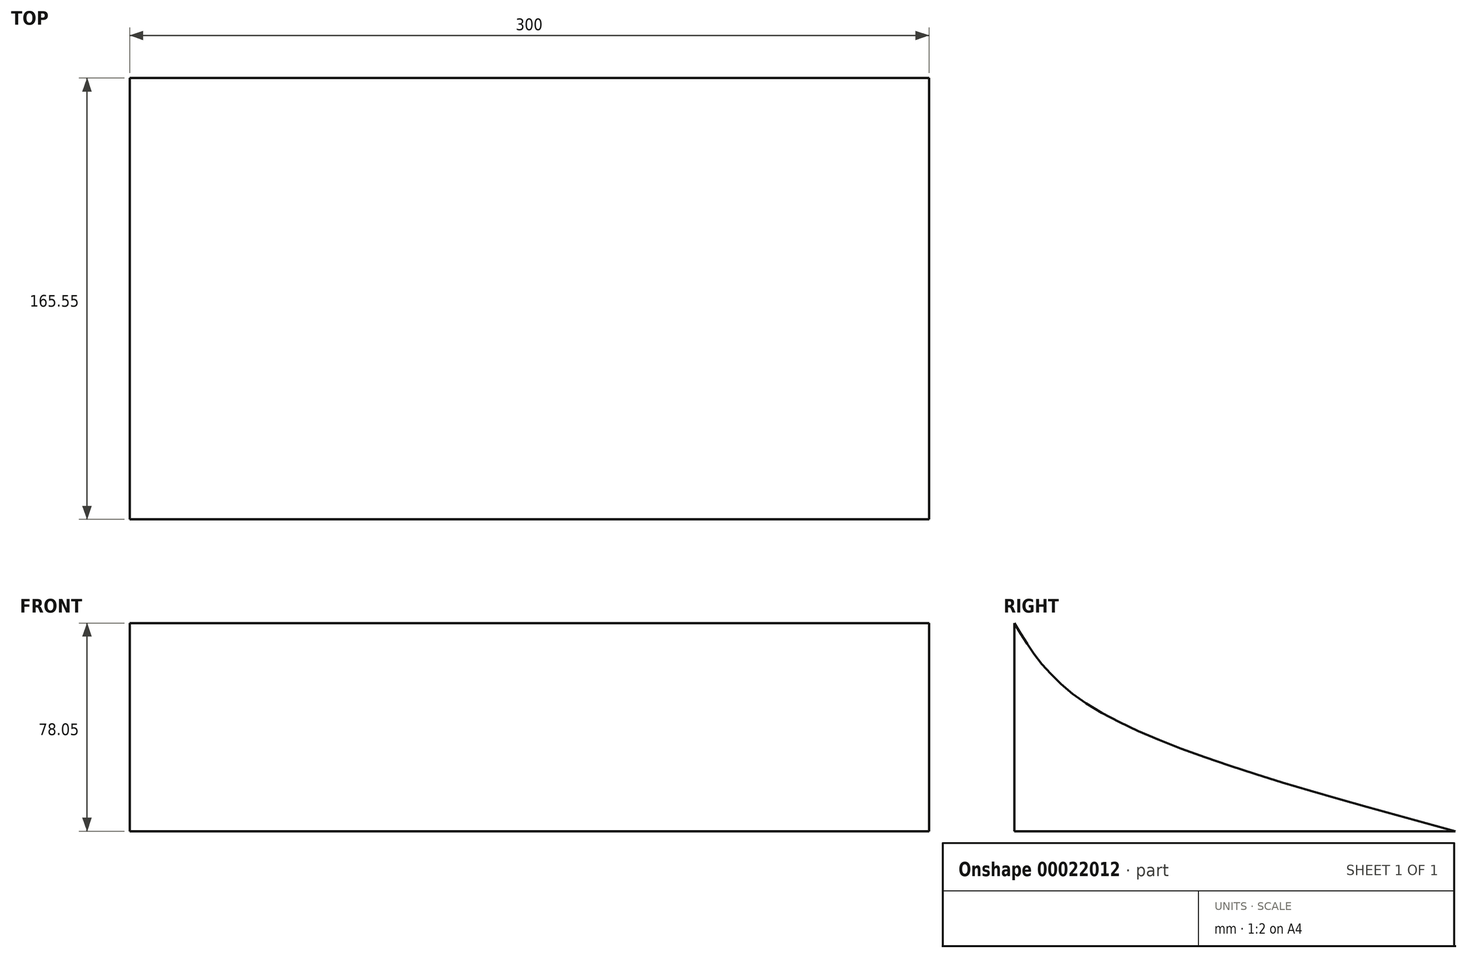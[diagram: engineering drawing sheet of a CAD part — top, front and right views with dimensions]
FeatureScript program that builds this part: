
annotation { "Feature Type Name" : "Feature", "Feature Type Description" : "" }
export const myFeature = defineFeature(function(context is Context, id is Id, definition is map)
    precondition{}
    {
        {
            var Q0;
            Q0=qCreatedBy(makeId("Right.planeOp"),FACE);
            var sketch = newSketch(context, id + "F0", { "sketchPlane" : qUnion([Q0])});
            skFitSpline(sketch, "E0", {"points": [v(0, 0) * mm, v(26.1, -29.47) * mm, v(165.55, -78.05) * mm], "startDerivative": vector(53.68, -88.74) * mm, "endDerivative": vector(255.91, -69.42) * mm});
            skLineSegment(sketch, "E1", {"start": v(165.55, -78.05) * mm, "end": v(6.1, -78.05) * mm});
            skLineSegment(sketch, "E2", {"start": v(0, 0) * mm, "end": v(0, -78.05) * mm});
            skLineSegment(sketch, "E3", {"start": v(0, -78.05) * mm, "end": v(6.1, -78.05) * mm});
            skSolve(sketch);
        }
        {
            var Q0;
            Q0 = qSketchRegion(id + "F0", true);
            extrude(context, id + "F1", {"entities" : qUnion([Q0]), "depth" : 300 * mm});
        }
    });
